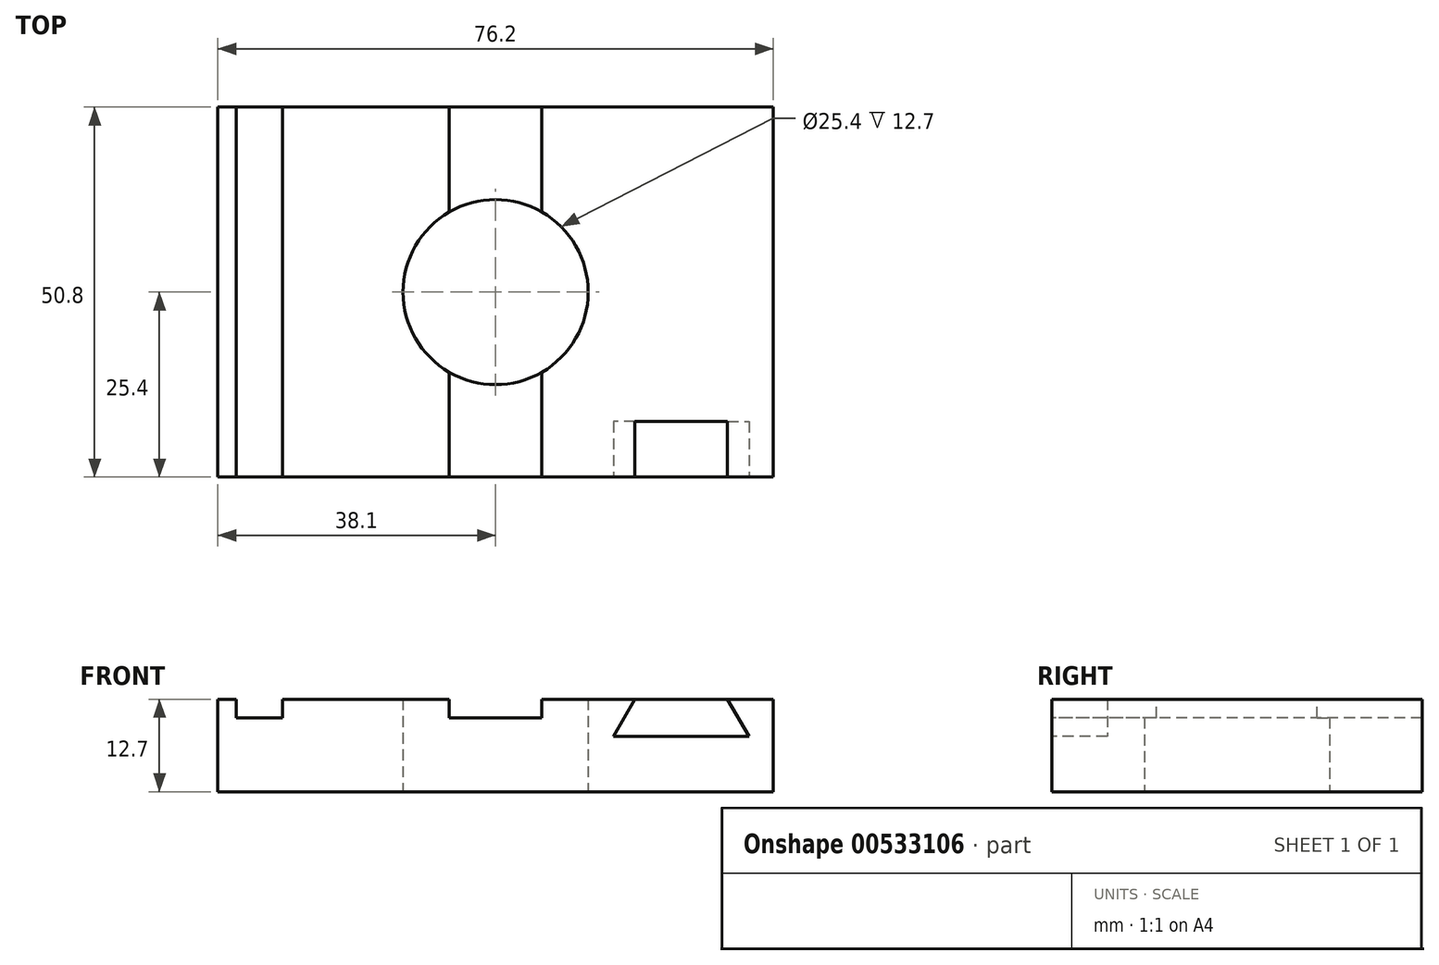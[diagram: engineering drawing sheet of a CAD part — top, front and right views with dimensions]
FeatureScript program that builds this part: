
annotation { "Feature Type Name" : "Feature", "Feature Type Description" : "" }
export const myFeature = defineFeature(function(context is Context, id is Id, definition is map)
    precondition{}
    {
        {
            var Q0;
            Q0=qCreatedBy(makeId("Top.planeOp"),FACE);
            var sketch = newSketch(context, id + "F0", { "sketchPlane" : qUnion([Q0])});
            skLineSegment(sketch, "E0.bottom", {"start": v(38.1, -25.4) * mm, "end": v(-38.1, -25.4) * mm});
            skLineSegment(sketch, "E0.top", {"start": v(38.1, 25.4) * mm, "end": v(-38.1, 25.4) * mm});
            skLineSegment(sketch, "E0.left", {"start": v(38.1, -25.4) * mm, "end": v(38.1, 25.4) * mm});
            skLineSegment(sketch, "E0.right", {"start": v(-38.1, -25.4) * mm, "end": v(-38.1, 25.4) * mm});
            skPoint(sketch, "E0.middle", {"position": v(0, 0) * mm});
            skCircle(sketch, "E1", {"center": v(0, 0) * mm, "radius": 12.7 * mm});
            skSolve(sketch);
        }
        {
            var Q0;
            Q0=makeQuery(id+"F0.imprint","IMPRINT",FACE,{"disambiguationData":[TD([[makeQuery(id+"F0.imprint","IMPRINT",EDGE,{"derivedFrom":sQuery(id+"F0.wireOp",EDGE,"E0.bottom")}),-1.0]])]});
            extrude(context, id + "F1", {"entities" : qUnion([Q0]), "depth" : 12.7 * mm, "offsetDistance" : 25.4 * mm});
        }
        {
            var Q0;
            Q0=makeQuery(id+"F1.opExtrude","CAP_FACE",FACE,{"disambiguationData":[OSD([sQuery(id+"F0.wireOp",EDGE,"E0.bottom"),sQuery(id+"F0.wireOp",EDGE,"E0.top"),sQuery(id+"F0.wireOp",EDGE,"E0.left"),sQuery(id+"F0.wireOp",EDGE,"E0.right"),sQuery(id+"F0.wireOp",EDGE,"E1")])],"isStart":false});
            var sketch = newSketch(context, id + "F2", { "sketchPlane" : qUnion([Q0])});
            skLineSegment(sketch, "E2.bottom", {"start": v(-35.56, 25.4) * mm, "end": v(-29.21, 25.4) * mm});
            skLineSegment(sketch, "E2.top", {"start": v(-35.56, -25.4) * mm, "end": v(-29.21, -25.4) * mm});
            skLineSegment(sketch, "E2.left", {"start": v(-35.56, 25.4) * mm, "end": v(-35.56, -25.4) * mm});
            skLineSegment(sketch, "E2.right", {"start": v(-29.21, 25.4) * mm, "end": v(-29.21, -25.4) * mm});
            skLineSegment(sketch, "E3.bottom", {"start": v(-6.35, 25.4) * mm, "end": v(6.35, 25.4) * mm});
            skLineSegment(sketch, "E3.top", {"start": v(-6.35, -25.4) * mm, "end": v(6.35, -25.4) * mm});
            skLineSegment(sketch, "E3.left", {"start": v(-6.35, 25.4) * mm, "end": v(-6.35, -25.4) * mm});
            skLineSegment(sketch, "E3.right", {"start": v(6.35, 25.4) * mm, "end": v(6.35, -25.4) * mm});
            skPoint(sketch, "E4", {"position": v(0, 0) * mm});
            skLineSegment(sketch, "E5", {"start": v(0, 25.4) * mm, "end": v(0, -25.4) * mm, "construction": true});
            skSolve(sketch);
        }
        {
            var Q0;
            Q0=makeQuery(id+"F2.imprint","IMPRINT",FACE,{"disambiguationData":[TD([[makeQuery(id+"F2.imprint","IMPRINT",EDGE,{"derivedFrom":sQuery(id+"F2.wireOp",EDGE,"E2.bottom")}),1.0]])]});
            var Q1;
            {var subQ0=sQuery(id+"F2.wireOp",EDGE,"E3.bottom");Q1=makeQuery(id+"F2.imprint","IMPRINT",FACE,{"disambiguationData":[TD([[makeQuery(id+"F2.imprint","IMPRINT",EDGE,{"derivedFrom":subQ0}),1.0]])]});}
            var Q2;
            {var subQ0=sQuery(id+"F2.wireOp",EDGE,"E3.top");Q2=makeQuery(id+"F2.imprint","IMPRINT",FACE,{"disambiguationData":[TD([[makeQuery(id+"F2.imprint","IMPRINT",EDGE,{"derivedFrom":subQ0}),-1.0]])]});}
            extrude(context, id + "F3", {"entities" : qUnion([Q0, Q1, Q2]), "operationType" : NewBodyOperationType.REMOVE, "oppositeDirection" : true, "depth" : 2.54 * mm, "offsetDistance" : 25.4 * mm});
        }
        {
            var Q0;
            Q0=makeQuery(id+"F1.opExtrude","SWEPT_FACE",FACE,{"disambiguationData":[OSD([sQuery(id+"F0.wireOp",EDGE,"E0.bottom")])]});
            var sketch = newSketch(context, id + "F4", { "sketchPlane" : qUnion([Q0])});
            skLineSegment(sketch, "E6", {"start": v(19.12, 12.7) * mm, "end": v(16.19, 7.62) * mm});
            skLineSegment(sketch, "E7", {"start": v(16.19, 7.62) * mm, "end": v(34.75, 7.62) * mm});
            skLineSegment(sketch, "E8", {"start": v(34.75, 7.62) * mm, "end": v(31.82, 12.7) * mm});
            skLineSegment(sketch, "E9", {"start": v(31.82, 12.7) * mm, "end": v(19.12, 12.7) * mm});
            skLineSegment(sketch, "E10", {"start": v(25.47, 7.62) * mm, "end": v(25.47, 12.7) * mm, "construction": true});
            skSolve(sketch);
        }
        {
            var Q0;
            Q0=makeQuery(id+"F4.imprint","IMPRINT",FACE,{"disambiguationData":[TD([[makeQuery(id+"F4.imprint","IMPRINT",EDGE,{"derivedFrom":sQuery(id+"F4.wireOp",EDGE,"E6")}),1.0]])]});
            extrude(context, id + "F5", {"entities" : qUnion([Q0]), "operationType" : NewBodyOperationType.REMOVE, "oppositeDirection" : true, "depth" : 7.62 * mm, "offsetDistance" : 25.4 * mm});
        }
    });
